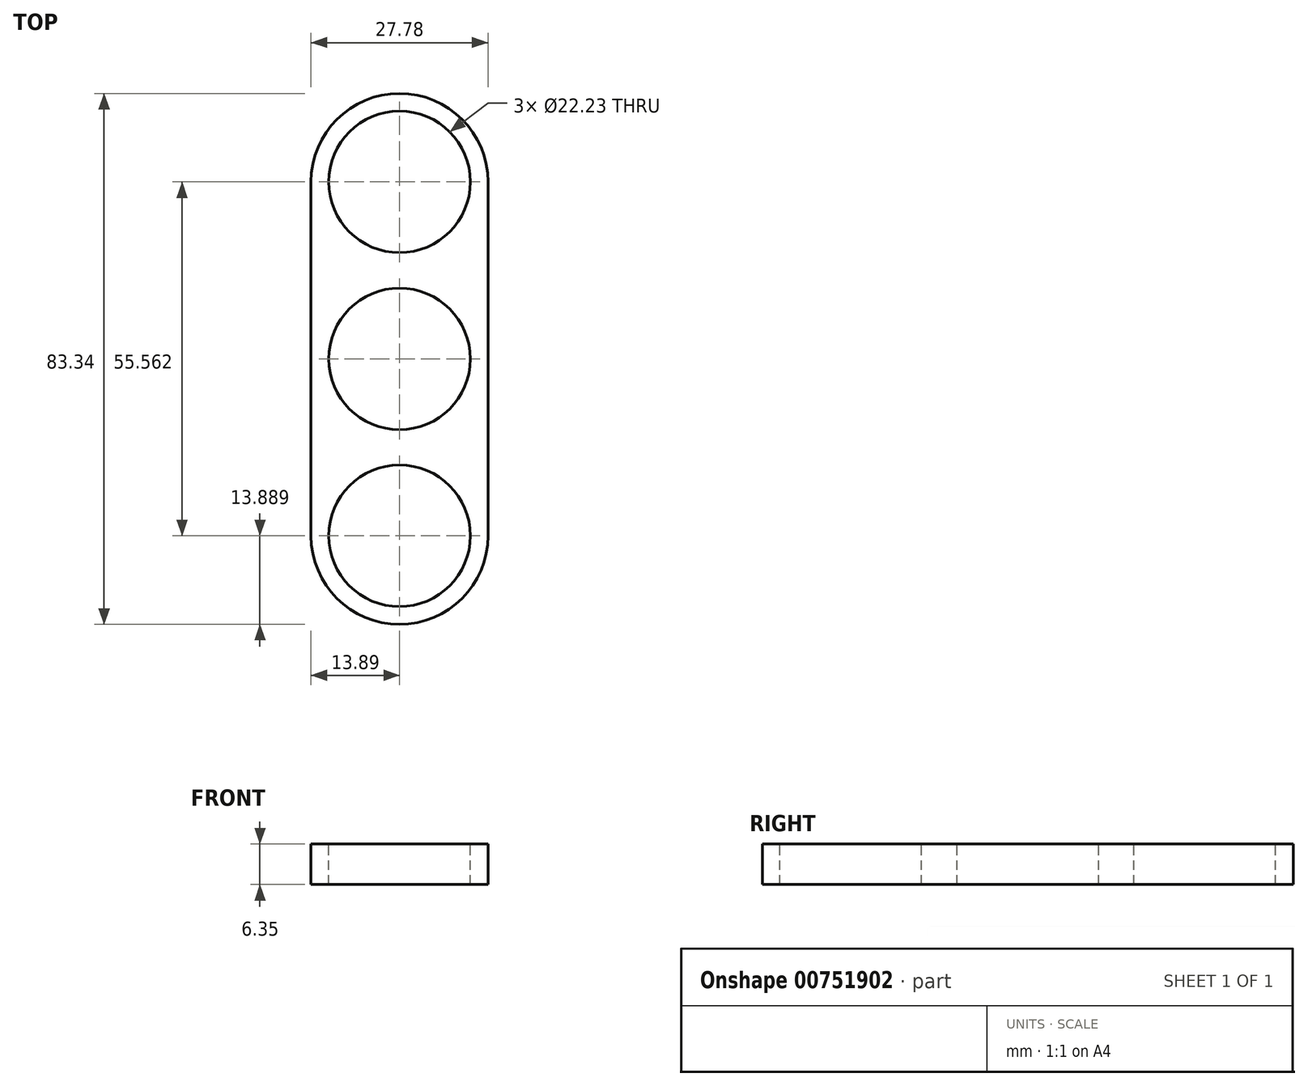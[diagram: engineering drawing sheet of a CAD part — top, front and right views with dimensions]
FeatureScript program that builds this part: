
annotation { "Feature Type Name" : "Feature", "Feature Type Description" : "" }
export const myFeature = defineFeature(function(context is Context, id is Id, definition is map)
    precondition{}
    {
        {
            var Q0;
            Q0=qCreatedBy(makeId("Top.planeOp"),FACE);
            var sketch = newSketch(context, id + "F0", { "sketchPlane" : qUnion([Q0])});
            skCircle(sketch, "E0", {"center": v(0, 0) * mm, "radius": 13.9 * mm});
            skCircle(sketch, "E1", {"center": v(0, 13.9) * mm, "radius": 13.9 * mm});
            skCircle(sketch, "E2", {"center": v(0, 27.78) * mm, "radius": 13.9 * mm});
            skCircle(sketch, "E3", {"center": v(0, -13.9) * mm, "radius": 13.9 * mm});
            skCircle(sketch, "E4", {"center": v(0, -27.78) * mm, "radius": 13.9 * mm});
            skLineSegment(sketch, "E5", {"start": v(0, 27.78) * mm, "end": v(-13.9, 27.78) * mm});
            skLineSegment(sketch, "E6", {"start": v(0, 27.78) * mm, "end": v(13.9, 27.78) * mm});
            skLineSegment(sketch, "E7", {"start": v(13.9, 27.78) * mm, "end": v(13.9, -27.78) * mm});
            skLineSegment(sketch, "E8", {"start": v(-13.9, 27.78) * mm, "end": v(-13.9, -27.78) * mm});
            skSolve(sketch);
        }
        {
            var Q0;
            Q0=qSketchRegion(id+"F0",true);
            var Q1;
            {var subQ2=sQuery(id+"F0.wireOp",EDGE,"E2");var subQ4=makeQuery(id+"F0.imprint","INTERSECT",VERTEX,{"derivedFrom":[sQuery(id+"F0.wireOp",EDGE,"E0"),subQ2]});Q1=makeQuery(id+"F0.imprint","IMPRINT",FACE,{"disambiguationData":[TD([[makeQuery(id+"F0.imprint","IMPRINT",EDGE,{"disambiguationData":[TD([[subQ4,1.0]])],"derivedFrom":subQ2}),1.0]])]});}
            var Q2;
            {var subQ0=sQuery(id+"F0.wireOp",EDGE,"E1");var subQ1=sQuery(id+"F0.wireOp",EDGE,"E0");var subQ2=makeQuery(id+"F0.imprint","INTERSECT",VERTEX,{"disambiguationData":[OD(0.0)],"derivedFrom":[subQ1,subQ0]});Q2=makeQuery(id+"F0.imprint","IMPRINT",FACE,{"disambiguationData":[TD([[makeQuery(id+"F0.imprint","IMPRINT",EDGE,{"disambiguationData":[TD([[subQ2,-1.0]])],"derivedFrom":subQ1}),1.0]])]});}
            var Q3;
            {var subQ0=sQuery(id+"F0.wireOp",EDGE,"E3");var subQ1=sQuery(id+"F0.wireOp",EDGE,"E0");var subQ2=makeQuery(id+"F0.imprint","INTERSECT",VERTEX,{"disambiguationData":[OD(0.0)],"derivedFrom":[subQ1,subQ0]});Q3=makeQuery(id+"F0.imprint","IMPRINT",FACE,{"disambiguationData":[TD([[makeQuery(id+"F0.imprint","IMPRINT",EDGE,{"disambiguationData":[TD([[subQ2,-1.0]])],"derivedFrom":subQ1}),1.0]])]});}
            var Q4;
            {var subQ0=sQuery(id+"F0.wireOp",EDGE,"E4");var subQ1=sQuery(id+"F0.wireOp",EDGE,"E3");var subQ2=makeQuery(id+"F0.imprint","INTERSECT",VERTEX,{"disambiguationData":[OD(0.0)],"derivedFrom":[subQ1,subQ0]});Q4=makeQuery(id+"F0.imprint","IMPRINT",FACE,{"disambiguationData":[TD([[makeQuery(id+"F0.imprint","IMPRINT",EDGE,{"disambiguationData":[TD([[subQ2,-1.0]])],"derivedFrom":subQ1}),1.0]])]});}
            extrude(context, id + "F1", {"entities" : qUnion([Q0, Q1, Q2, Q3, Q4]), "depth" : 6.35 * mm, "offsetDistance" : 25.4 * mm});
        }
        {
            var Q0;
            Q0=makeQuery(id+"F1.opExtrude","CAP_FACE",FACE,{"disambiguationData":[OSD([sQuery(id+"F0.wireOp",EDGE,"E2"),sQuery(id+"F0.wireOp",EDGE,"E4"),sQuery(id+"F0.wireOp",EDGE,"E7"),sQuery(id+"F0.wireOp",EDGE,"E8")])],"isStart":false});
            var sketch = newSketch(context, id + "F2", { "sketchPlane" : qUnion([Q0])});
            skLineSegment(sketch, "E9", {"start": v(0, 41.67) * mm, "end": v(0, 27.78) * mm});
            skLineSegment(sketch, "E10", {"start": v(0, -41.67) * mm, "end": v(0, -27.78) * mm});
            skCircle(sketch, "E11", {"center": v(0, 27.78) * mm, "radius": 11.11 * mm});
            skCircle(sketch, "E12", {"center": v(0, 0) * mm, "radius": 11.11 * mm});
            skCircle(sketch, "E13", {"center": v(0, -27.78) * mm, "radius": 11.11 * mm});
            skSolve(sketch);
        }
        {
            var Q0;
            Q0=qSketchRegion(id+"F2",true);
            extrude(context, id + "F3", {"entities" : qUnion([Q0]), "operationType" : NewBodyOperationType.REMOVE, "oppositeDirection" : true, "depth" : 25.4 * mm, "offsetDistance" : 25.4 * mm});
        }
    });
